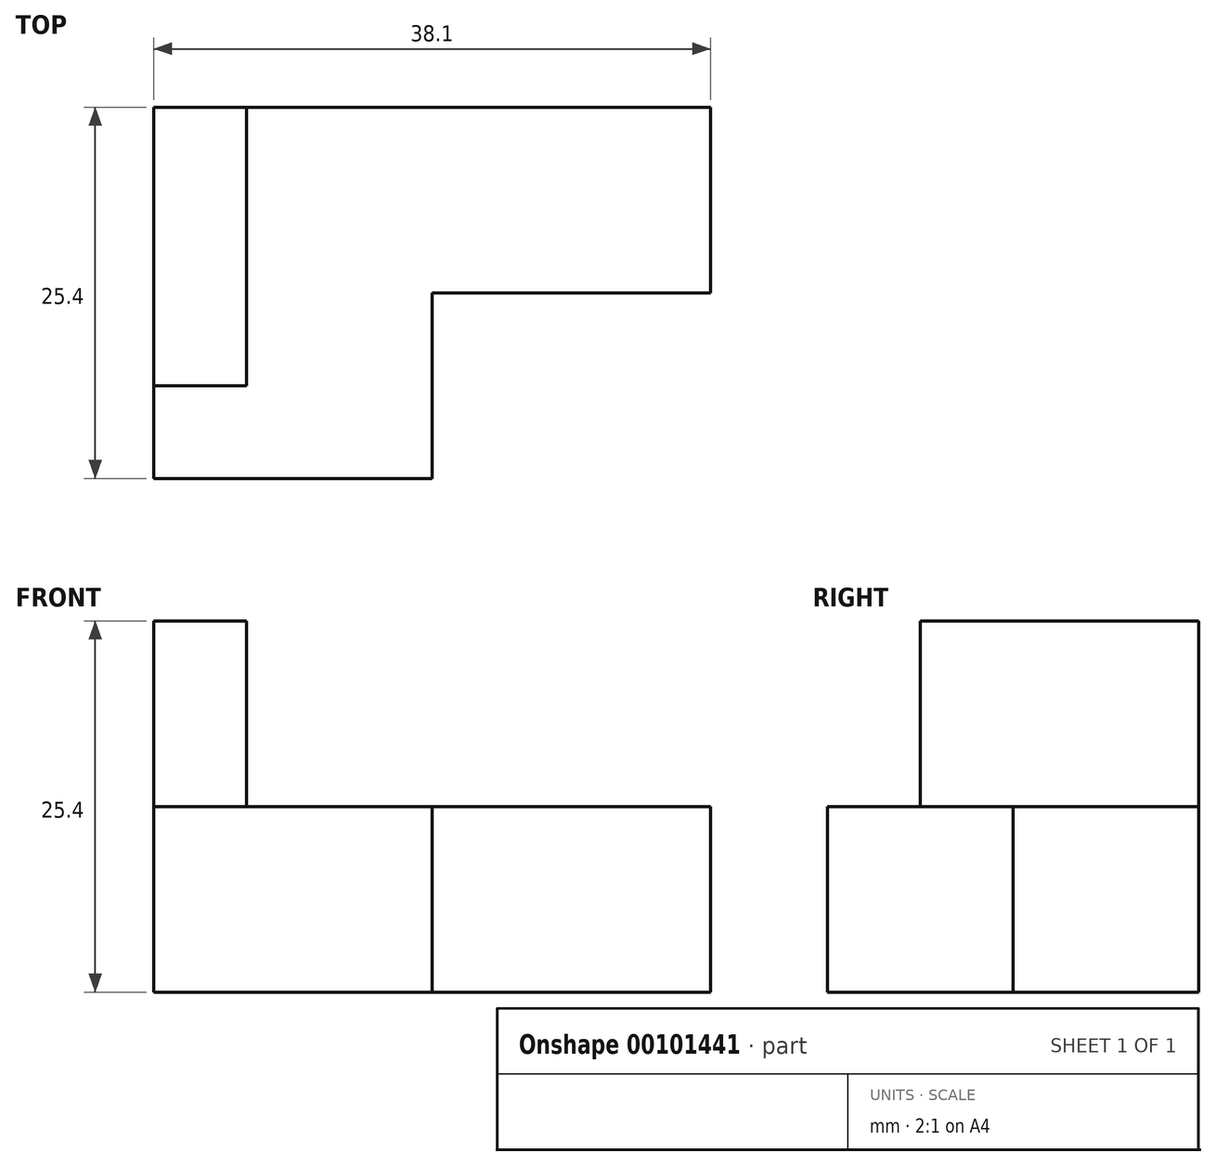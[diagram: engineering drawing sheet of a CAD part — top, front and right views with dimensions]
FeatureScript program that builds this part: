
annotation { "Feature Type Name" : "Feature", "Feature Type Description" : "" }
export const myFeature = defineFeature(function(context is Context, id is Id, definition is map)
    precondition{}
    {
        {
            var Q0;
            Q0=qCreatedBy(makeId("Top.planeOp"),FACE);
            var sketch = newSketch(context, id + "F0", { "sketchPlane" : qUnion([Q0])});
            skLineSegment(sketch, "E0", {"start": v(0, 0) * mm, "end": v(38.1, 0) * mm});
            skLineSegment(sketch, "E1", {"start": v(38.1, 0) * mm, "end": v(38.1, -12.7) * mm});
            skLineSegment(sketch, "E2", {"start": v(38.1, -12.7) * mm, "end": v(19.05, -12.7) * mm});
            skLineSegment(sketch, "E3", {"start": v(19.05, -12.7) * mm, "end": v(19.05, -25.4) * mm});
            skLineSegment(sketch, "E4", {"start": v(19.05, -25.4) * mm, "end": v(0, -25.4) * mm});
            skLineSegment(sketch, "E5", {"start": v(0, -25.4) * mm, "end": v(0, 0) * mm});
            skSolve(sketch);
        }
        {
            var Q0;
            Q0 = qSketchRegion(id + "F0", true);
            extrude(context, id + "F1", {"entities" : qUnion([Q0]), "depth" : 12.7 * mm});
        }
        {
            var Q0;
            Q0=makeQuery(id+"F1.opExtrude","CAP_FACE",FACE,{"disambiguationData":[OSD([sQuery(id+"F0.wireOp",EDGE,"E0"),sQuery(id+"F0.wireOp",EDGE,"E1"),sQuery(id+"F0.wireOp",EDGE,"E2"),sQuery(id+"F0.wireOp",EDGE,"E3"),sQuery(id+"F0.wireOp",EDGE,"E4"),sQuery(id+"F0.wireOp",EDGE,"E5")])],"isStart":false});
            var sketch = newSketch(context, id + "F2", { "sketchPlane" : qUnion([Q0])});
            skLineSegment(sketch, "E6", {"start": v(0, 0) * mm, "end": v(0, -19.05) * mm});
            skLineSegment(sketch, "E7", {"start": v(0, -19.05) * mm, "end": v(6.35, -19.05) * mm});
            skLineSegment(sketch, "E8", {"start": v(6.35, -19.05) * mm, "end": v(6.35, 0) * mm});
            skLineSegment(sketch, "E9", {"start": v(6.35, 0) * mm, "end": v(0, 0) * mm});
            skSolve(sketch);
        }
        {
            var Q0;
            Q0 = qSketchRegion(id + "F2", true);
            extrude(context, id + "F3", {"entities" : qUnion([Q0]), "operationType" : NewBodyOperationType.ADD, "depth" : 12.7 * mm});
        }
    });
